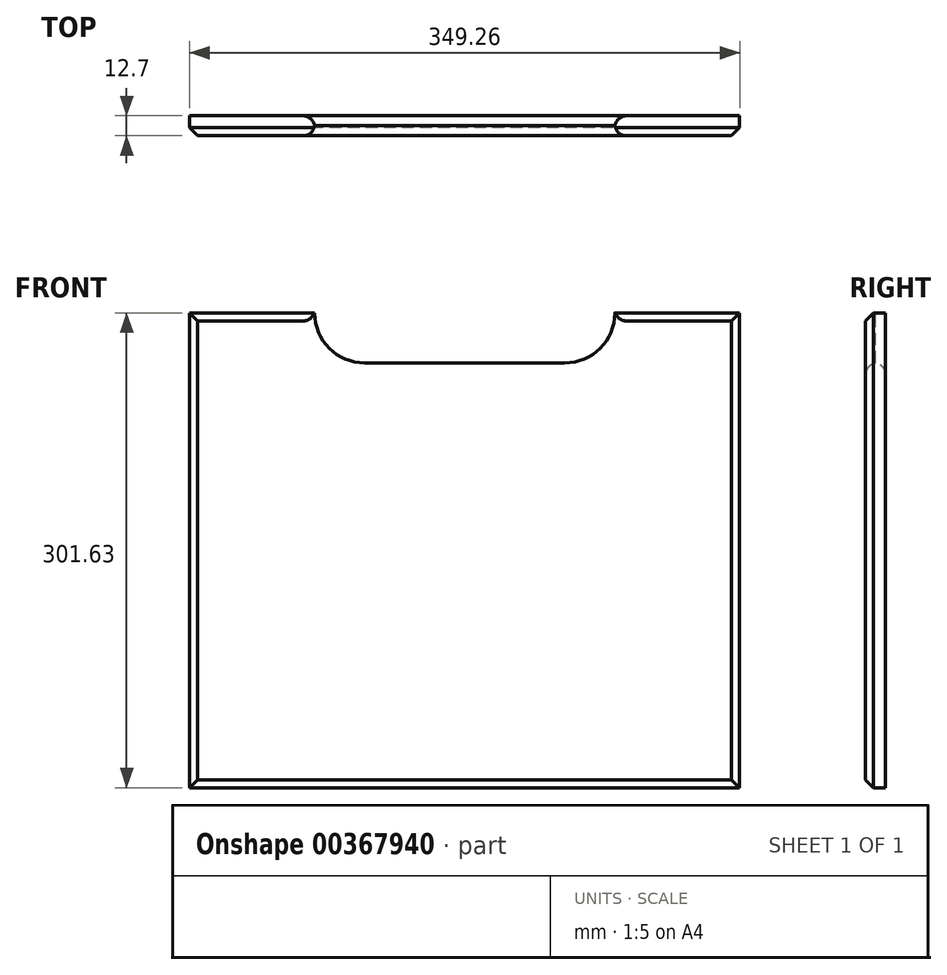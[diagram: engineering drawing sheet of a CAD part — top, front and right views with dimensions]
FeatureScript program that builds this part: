
annotation { "Feature Type Name" : "Feature", "Feature Type Description" : "" }
export const myFeature = defineFeature(function(context is Context, id is Id, definition is map)
    precondition{}
    {
        {
            var Q0;
            Q0=qCreatedBy(makeId("Front.planeOp"),FACE);
            var sketch = newSketch(context, id + "F0", { "sketchPlane" : qUnion([Q0])});
            skLineSegment(sketch, "E0.bottom", {"start": v(-174.63, 80.82) * mm, "end": v(-95.25, 80.82) * mm});
            skLineSegment(sketch, "E0.top", {"start": v(-174.63, -220.8) * mm, "end": v(174.62, -220.8) * mm});
            skLineSegment(sketch, "E0.left", {"start": v(-174.63, 80.82) * mm, "end": v(-174.63, -220.8) * mm});
            skLineSegment(sketch, "E0.right", {"start": v(174.62, 80.82) * mm, "end": v(174.62, -220.8) * mm});
            skArc(sketch, "E1.0.startCap", {"start": v(-63.5, 49.07) * mm, "mid": v(-85.95, 58.37) * mm, "end": v(-95.25, 80.82) * mm});
            skArc(sketch, "E1.0.endCap", {"start": v(95.25, 80.82) * mm, "mid": v(85.95, 58.37) * mm, "end": v(63.5, 49.07) * mm});
            skLineSegment(sketch, "E1.0.right", {"start": v(-63.5, 49.07) * mm, "end": v(63.5, 49.07) * mm});
            skLineSegment(sketch, "E2.trimOffspring", {"start": v(95.25, 80.82) * mm, "end": v(174.62, 80.82) * mm});
            skSolve(sketch);
        }
        {
            var Q0;
            Q0=makeQuery(id+"F0.imprint","IMPRINT",FACE,{"disambiguationData":[TD([[makeQuery(id+"F0.imprint","IMPRINT",EDGE,{"derivedFrom":sQuery(id+"F0.wireOp",EDGE,"E0.bottom")}),-1.0]])]});
            extrude(context, id + "F1", {"entities" : qUnion([Q0]), "depth" : 12.7 * mm});
        }
        {
            var Q0;
            Q0=makeQuery(id+"F1.opExtrude","CAP_EDGE",EDGE,{"disambiguationData":[OSD([sQuery(id+"F0.wireOp",EDGE,"E1.0.right")])],"isStart":false});
            var Q1;
            Q1=makeQuery(id+"F1.opExtrude","CAP_EDGE",EDGE,{"disambiguationData":[OSD([sQuery(id+"F0.wireOp",EDGE,"E1.0.right")])],"isStart":true});
            fillet(context, id + "F2", {"entities" : qUnion([Q0, Q1]), "radius" : 7.62 * mm, "tangentPropagation" : true, "allowEdgeOverflow" : false});
        }
        {
            var Q0;
            Q0=makeQuery(id+"F1.opExtrude","CAP_EDGE",EDGE,{"disambiguationData":[OSD([sQuery(id+"F0.wireOp",EDGE,"E0.bottom")])],"isStart":false});
            var Q1;
            Q1=makeQuery(id+"F1.opExtrude","CAP_EDGE",EDGE,{"disambiguationData":[OSD([sQuery(id+"F0.wireOp",EDGE,"E0.left")])],"isStart":false});
            var Q2;
            Q2=makeQuery(id+"F1.opExtrude","CAP_EDGE",EDGE,{"disambiguationData":[OSD([sQuery(id+"F0.wireOp",EDGE,"E0.top")])],"isStart":false});
            var Q3;
            Q3=makeQuery(id+"F1.opExtrude","CAP_EDGE",EDGE,{"disambiguationData":[OSD([sQuery(id+"F0.wireOp",EDGE,"E2.trimOffspring")])],"isStart":false});
            var Q4;
            Q4=makeQuery(id+"F1.opExtrude","CAP_EDGE",EDGE,{"disambiguationData":[OSD([sQuery(id+"F0.wireOp",EDGE,"E0.right")])],"isStart":false});
            chamfer(context, id + "F3", {"entities" : qUnion([Q0, Q1, Q2, Q3, Q4]), "width" : 5.08 * mm});
        }
    });
